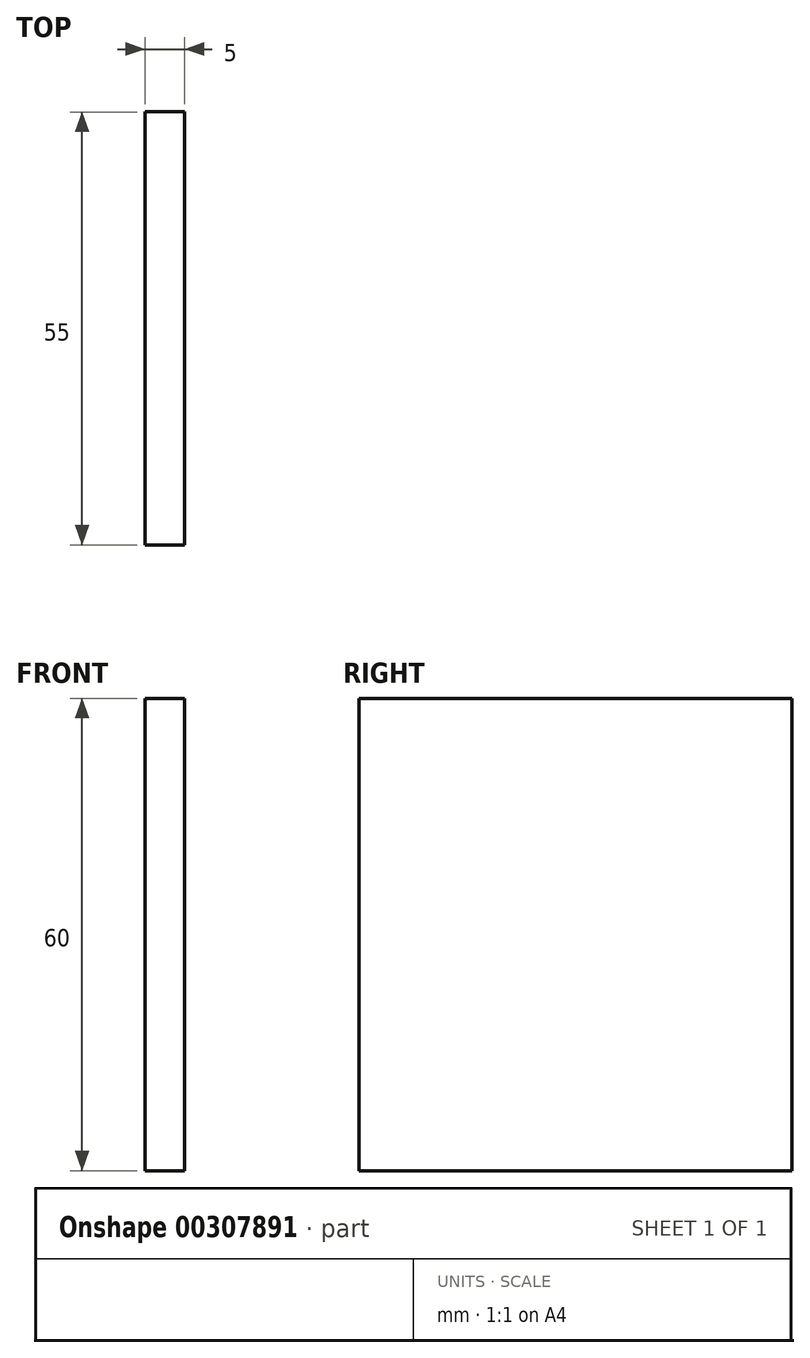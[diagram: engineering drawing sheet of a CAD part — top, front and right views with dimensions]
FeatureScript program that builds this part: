
annotation { "Feature Type Name" : "Feature", "Feature Type Description" : "" }
export const myFeature = defineFeature(function(context is Context, id is Id, definition is map)
    precondition{}
    {
        {
            var Q0;
            Q0=qCreatedBy(makeId("Right.planeOp"),FACE);
            var sketch = newSketch(context, id + "F0", { "sketchPlane" : qUnion([Q0])});
            skLineSegment(sketch, "E0.bottom", {"start": v(-35.54, 12.09) * mm, "end": v(19.46, 12.09) * mm});
            skLineSegment(sketch, "E0.top", {"start": v(-35.54, -47.91) * mm, "end": v(19.46, -47.91) * mm});
            skLineSegment(sketch, "E0.left", {"start": v(-35.54, 12.09) * mm, "end": v(-35.54, -47.91) * mm});
            skLineSegment(sketch, "E0.right", {"start": v(19.46, 12.09) * mm, "end": v(19.46, -47.91) * mm});
            skSolve(sketch);
        }
        {
            var Q0;
            Q0=makeQuery(id+"F0.imprint","IMPRINT",FACE,{"disambiguationData":[TD([[makeQuery(id+"F0.imprint","IMPRINT",EDGE,{"derivedFrom":sQuery(id+"F0.wireOp",EDGE,"E0.bottom")}),-1.0]])]});
            extrude(context, id + "F1", {"entities" : qUnion([Q0]), "depth" : 5 * mm});
        }
    });
